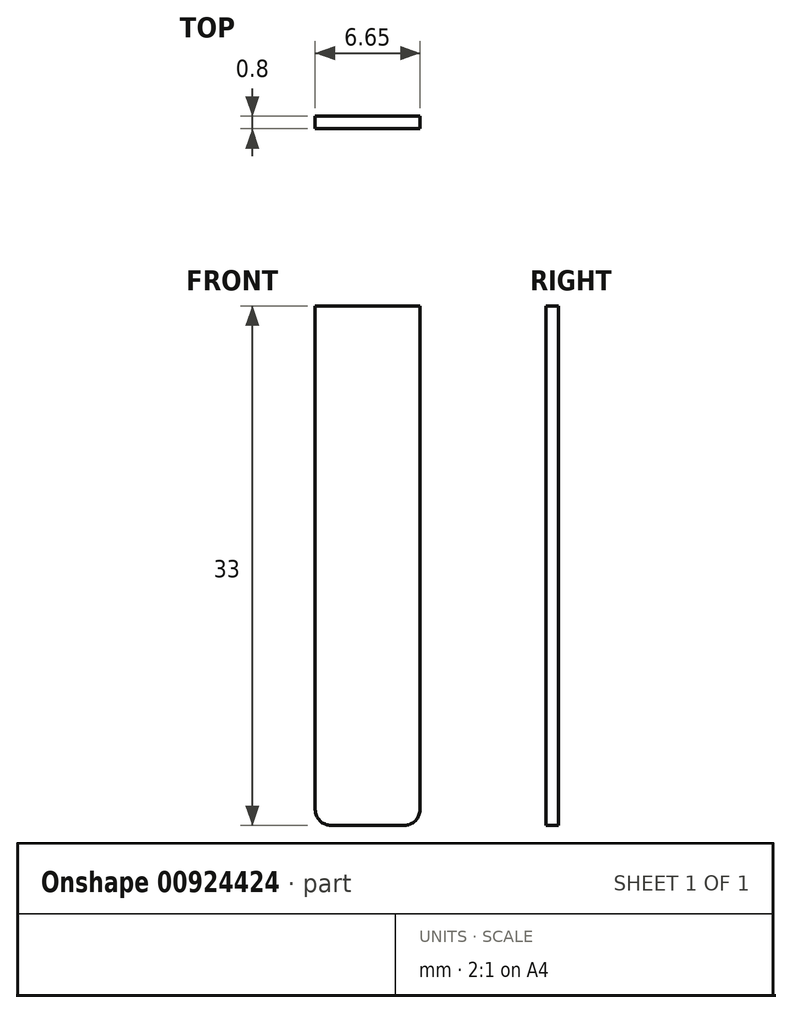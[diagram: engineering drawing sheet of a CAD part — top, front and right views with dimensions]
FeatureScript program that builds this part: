
annotation { "Feature Type Name" : "Feature", "Feature Type Description" : "" }
export const myFeature = defineFeature(function(context is Context, id is Id, definition is map)
    precondition{}
    {
        {
            var Q0;
            Q0=qCreatedBy(makeId("Front.planeOp"),FACE);
            var sketch = newSketch(context, id + "F0", { "sketchPlane" : qUnion([Q0])});
            skLineSegment(sketch, "E0.bottom", {"start": v(0, 0) * mm, "end": v(6.65, 0) * mm});
            skLineSegment(sketch, "E0.top", {"start": v(0, 33) * mm, "end": v(6.65, 33) * mm});
            skLineSegment(sketch, "E0.left", {"start": v(0, 0) * mm, "end": v(0, 33) * mm});
            skLineSegment(sketch, "E0.right", {"start": v(6.65, 0) * mm, "end": v(6.65, 33) * mm});
            skSolve(sketch);
        }
        {
            var Q0;
            Q0=makeQuery(id+"F0.imprint","IMPRINT",FACE,{"disambiguationData":[TD([[makeQuery(id+"F0.imprint","IMPRINT",EDGE,{"derivedFrom":sQuery(id+"F0.wireOp",EDGE,"E0.bottom")}),1.0]])]});
            extrude(context, id + "F1", {"entities" : qUnion([Q0]), "depth" : .8 * mm, "offsetDistance" : 25 * mm});
        }
        {
            var Q0;
            Q0=makeQuery(id+"F1.opExtrude","SWEPT_EDGE",EDGE,{"disambiguationData":[OSD([sQuery(id+"F0.wireOp",EDGE,"E0.bottom"),sQuery(id+"F0.wireOp",EDGE,"E0.right")])]});
            var Q1;
            Q1=makeQuery(id+"F1.opExtrude","SWEPT_EDGE",EDGE,{"disambiguationData":[OSD([sQuery(id+"F0.wireOp",EDGE,"E0.bottom"),sQuery(id+"F0.wireOp",EDGE,"E0.left")])]});
            fillet(context, id + "F2", {"entities" : qUnion([Q0, Q1]), "radius" : 1 * mm, "tangentPropagation" : true, "allowEdgeOverflow" : false});
        }
    });
